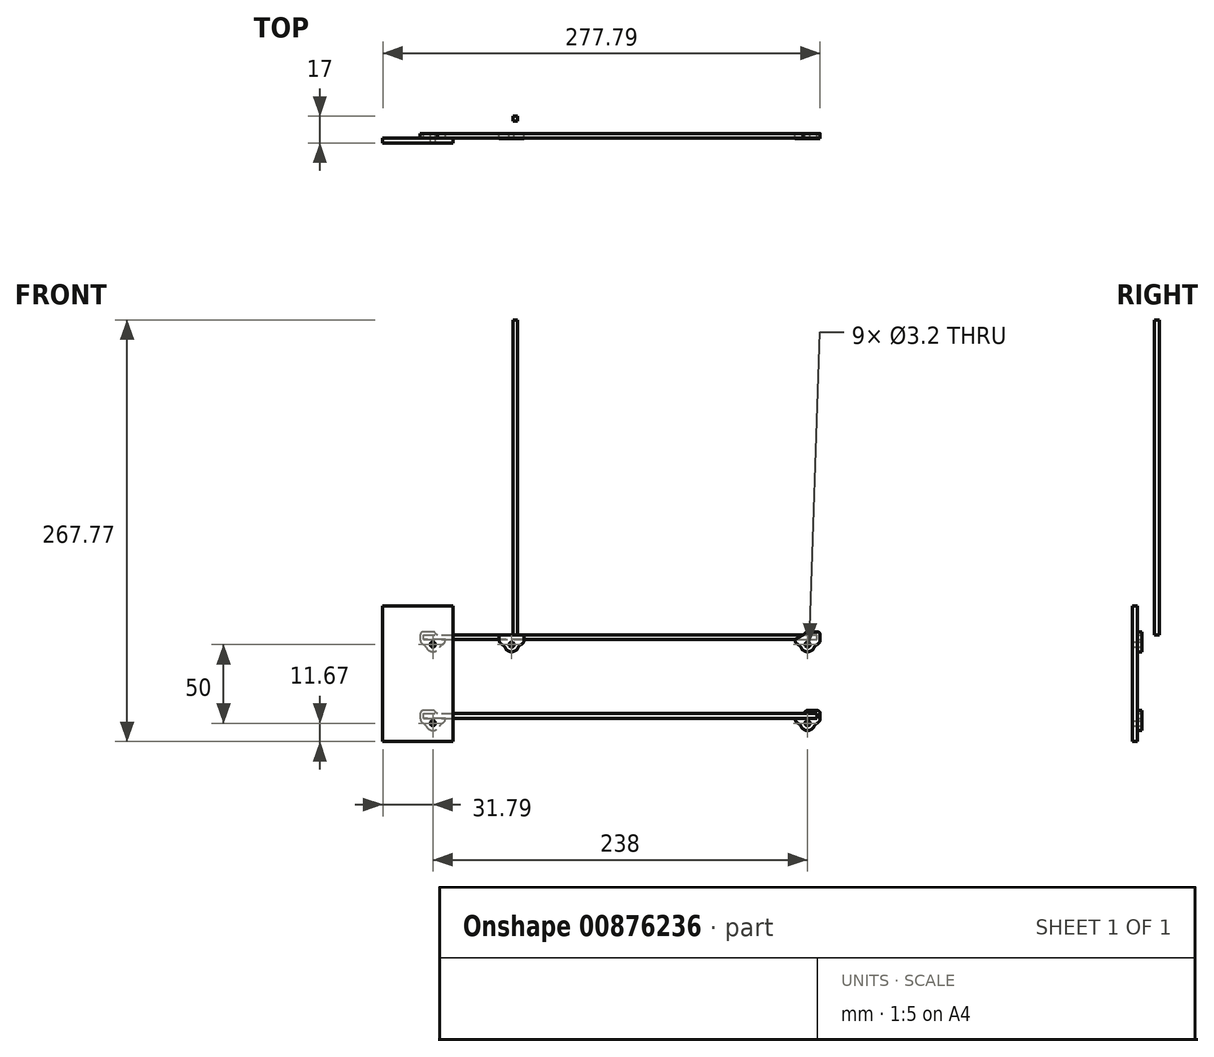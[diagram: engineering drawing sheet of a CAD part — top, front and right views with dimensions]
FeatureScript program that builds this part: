
annotation { "Feature Type Name" : "Feature", "Feature Type Description" : "" }
export const myFeature = defineFeature(function(context is Context, id is Id, definition is map)
    precondition{}
    {
        {
            var Q0;
            Q0=qCreatedBy(makeId("Front.planeOp"),FACE);
            var sketch = newSketch(context, id + "F0", { "sketchPlane" : qUnion([Q0])});
            skLineSegment(sketch, "E0", {"start": v(0, 0) * mm, "end": v(-238, 0) * mm});
            skLineSegment(sketch, "E1", {"start": v(0, -50) * mm, "end": v(-238, -50) * mm});
            skLineSegment(sketch, "E2", {"start": v(-238, -50) * mm, "end": v(-238, 188) * mm});
            skLineSegment(sketch, "E3", {"start": v(-188, 0) * mm, "end": v(-188, 188) * mm});
            skLineSegment(sketch, "E4", {"start": v(-188, 188) * mm, "end": v(-238, 188) * mm, "construction": true});
            skLineSegment(sketch, "E5", {"start": v(0, -50) * mm, "end": v(0, 0) * mm, "construction": true});
            skLineSegment(sketch, "E6", {"start": v(-188, 188) * mm, "end": v(-426, 188) * mm});
            skLineSegment(sketch, "E7", {"start": v(0, 0) * mm, "end": v(-188, 0) * mm});
            skSolve(sketch);
        }
        {
            var Q0;
            Q0=qCreatedBy(makeId("Front.planeOp"),FACE);
            var sketch = newSketch(context, id + "F1", { "sketchPlane" : qUnion([Q0])});
            skCircle(sketch, "E8", {"center": v(0, 0) * mm, "radius": 1.6 * mm});
            skArc(sketch, "E9", {"start": v(-4.15, -1.98) * mm, "mid": v(-2.46, -3.89) * mm, "end": v(0, -4.6) * mm});
            skLineSegment(sketch, "E10", {"start": v(-8, 3.1) * mm, "end": v(0, 3.1) * mm});
            skArc(sketch, "E11", {"start": v(-4.15, -1.98) * mm, "mid": v(-4.96, -0.83) * mm, "end": v(-6.09, 0) * mm});
            skArc(sketch, "E12", {"start": v(-6.09, 0) * mm, "mid": v(-7.48, 1.28) * mm, "end": v(-8, 3.1) * mm});
            skLineSegment(sketch, "E13.MirrorCS", {"start": v(8, 3.1) * mm, "end": v(0, 3.1) * mm});
            skArc(sketch, "E14.MirrorCS", {"start": v(6.09, 0) * mm, "mid": v(7.48, 1.28) * mm, "end": v(8, 3.1) * mm});
            skArc(sketch, "E15.MirrorCS", {"start": v(4.15, -1.98) * mm, "mid": v(4.96, -0.83) * mm, "end": v(6.09, 0) * mm});
            skArc(sketch, "E16.MirrorCS", {"start": v(4.15, -1.98) * mm, "mid": v(2.46, -3.89) * mm, "end": v(0, -4.6) * mm});
            skSolve(sketch);
        }
        {
            var Q0;
            Q0=makeQuery(id+"F1.imprint","IMPRINT",FACE,{"disambiguationData":[TD([[makeQuery(id+"F1.imprint","IMPRINT",EDGE,{"derivedFrom":sQuery(id+"F1.wireOp",EDGE,"E8")}),-1.0]])]});
            extrude(context, id + "F2", {"entities" : qUnion([Q0]), "depth" : 3 * mm, "offsetDistance" : 25 * mm});
        }
        {
            var Q0;
            Q0=qCreatedBy(makeId("Front.planeOp"),FACE);
            var sketch = newSketch(context, id + "F3", { "sketchPlane" : qUnion([Q0])});
            skCircle(sketch, "E17", {"center": v(0, 0) * mm, "radius": 1.6 * mm});
            skLineSegment(sketch, "E18", {"start": v(-8, 3.1) * mm, "end": v(6, 3.1) * mm});
            skLineSegment(sketch, "E19", {"start": v(6, 3.1) * mm, "end": v(6, 6.1) * mm});
            skLineSegment(sketch, "E20", {"start": v(6, 6.1) * mm, "end": v(-2.83, 6.1) * mm});
            skLineSegment(sketch, "E21", {"start": v(0, 8.1) * mm, "end": v(6, 8.1) * mm});
            skArc(sketch, "E22", {"start": v(8, 6.1) * mm, "mid": v(7.41, 7.51) * mm, "end": v(6, 8.1) * mm});
            skArc(sketch, "E23.0", {"start": v(-6.09, 0) * mm, "mid": v(-7.48, 1.28) * mm, "end": v(-8, 3.1) * mm});
            skArc(sketch, "E23.1", {"start": v(-4.15, -1.98) * mm, "mid": v(-4.96, -0.83) * mm, "end": v(-6.09, 0) * mm});
            skArc(sketch, "E23.2", {"start": v(-4.15, -1.98) * mm, "mid": v(-2.46, -3.89) * mm, "end": v(0, -4.6) * mm});
            skArc(sketch, "E24", {"start": v(0, 8.1) * mm, "mid": v(-0.77, 7.95) * mm, "end": v(-1.41, 7.51) * mm});
            skLineSegment(sketch, "E25", {"start": v(-1.41, 7.51) * mm, "end": v(-2.83, 6.1) * mm});
            skArc(sketch, "E26.0", {"start": v(4.15, -1.98) * mm, "mid": v(2.46, -3.89) * mm, "end": v(0, -4.6) * mm});
            skArc(sketch, "E26.1", {"start": v(4.15, -1.98) * mm, "mid": v(4.96, -0.83) * mm, "end": v(6.09, 0) * mm});
            skArc(sketch, "E26.2", {"start": v(6.09, 0) * mm, "mid": v(7.48, 1.28) * mm, "end": v(8, 3.1) * mm});
            skLineSegment(sketch, "E27", {"start": v(8, 6.1) * mm, "end": v(8, 3.1) * mm});
            skPoint(sketch, "E28.0", {"position": v(-119, 0) * mm});
            skPoint(sketch, "E28.1", {"position": v(-119, -50) * mm});
            skLineSegment(sketch, "E29", {"start": v(-119, 0) * mm, "end": v(-119, -50) * mm, "construction": true});
            skLineSegment(sketch, "E30.MirrorCS", {"start": v(-236.59, 7.51) * mm, "end": v(-235.17, 6.1) * mm});
            skCircle(sketch, "E31.MirrorC", {"center": v(-238, 0) * mm, "radius": 1.6 * mm});
            skLineSegment(sketch, "E32.MirrorCS", {"start": v(-244, 3.1) * mm, "end": v(-244, 6.1) * mm});
            skArc(sketch, "E33.MirrorCS", {"start": v(-242.15, -1.98) * mm, "mid": v(-242.96, -0.83) * mm, "end": v(-244.09, 0) * mm});
            skLineSegment(sketch, "E34.MirrorCS", {"start": v(-246, 6.1) * mm, "end": v(-246, 3.1) * mm});
            skArc(sketch, "E35.MirrorCS", {"start": v(-231.91, 0) * mm, "mid": v(-230.52, 1.28) * mm, "end": v(-230, 3.1) * mm});
            skArc(sketch, "E36.MirrorCS", {"start": v(-238, 8.1) * mm, "mid": v(-237.23, 7.95) * mm, "end": v(-236.59, 7.51) * mm});
            skArc(sketch, "E37.MirrorCS", {"start": v(-244.09, 0) * mm, "mid": v(-245.48, 1.28) * mm, "end": v(-246, 3.1) * mm});
            skArc(sketch, "E38.MirrorCS", {"start": v(-233.85, -1.98) * mm, "mid": v(-233.04, -0.83) * mm, "end": v(-231.91, 0) * mm});
            skArc(sketch, "E39.MirrorCS", {"start": v(-246, 6.1) * mm, "mid": v(-245.41, 7.51) * mm, "end": v(-244, 8.1) * mm});
            skLineSegment(sketch, "E40.MirrorCS", {"start": v(-244, 6.1) * mm, "end": v(-235.17, 6.1) * mm});
            skLineSegment(sketch, "E41.MirrorCS", {"start": v(-238, 8.1) * mm, "end": v(-244, 8.1) * mm});
            skLineSegment(sketch, "E42.MirrorCS", {"start": v(-230, 3.1) * mm, "end": v(-244, 3.1) * mm});
            skArc(sketch, "E43.MirrorCS", {"start": v(-233.85, -1.98) * mm, "mid": v(-235.54, -3.89) * mm, "end": v(-238, -4.6) * mm});
            skArc(sketch, "E44.MirrorCS", {"start": v(-242.15, -1.98) * mm, "mid": v(-240.46, -3.89) * mm, "end": v(-238, -4.6) * mm});
            skSolve(sketch);
        }
        {
            var Q0;
            Q0=makeQuery(id+"F3.imprint","IMPRINT",FACE,{"disambiguationData":[TD([[makeQuery(id+"F3.imprint","IMPRINT",EDGE,{"derivedFrom":sQuery(id+"F3.wireOp",EDGE,"E17")}),-1.0]])]});
            extrude(context, id + "F4", {"entities" : qUnion([Q0]), "depth" : 3 * mm, "offsetDistance" : 25 * mm});
        }
        {
            var Q0;
            Q0=makeQuery(id+"F3.imprint","IMPRINT",FACE,{"disambiguationData":[TD([[makeQuery(id+"F3.imprint","IMPRINT",EDGE,{"derivedFrom":sQuery(id+"F3.wireOp",EDGE,"E30.MirrorCS")}),-1.0]])]});
            var Q1;
            Q1=makeQuery(id+"F4.opExtrude","CAP_FACE",FACE,{"disambiguationData":[OSD([sQuery(id+"F3.wireOp",EDGE,"E17"),sQuery(id+"F3.wireOp",EDGE,"E18"),sQuery(id+"F3.wireOp",EDGE,"E19"),sQuery(id+"F3.wireOp",EDGE,"E20"),sQuery(id+"F3.wireOp",EDGE,"E21"),sQuery(id+"F3.wireOp",EDGE,"E22"),sQuery(id+"F3.wireOp",EDGE,"E23.0"),sQuery(id+"F3.wireOp",EDGE,"E23.1"),sQuery(id+"F3.wireOp",EDGE,"E23.2"),sQuery(id+"F3.wireOp",EDGE,"E24"),sQuery(id+"F3.wireOp",EDGE,"E25"),sQuery(id+"F3.wireOp",EDGE,"E26.0"),sQuery(id+"F3.wireOp",EDGE,"E26.1"),sQuery(id+"F3.wireOp",EDGE,"E26.2"),sQuery(id+"F3.wireOp",EDGE,"E27")])],"isStart":false});
            extrude(context, id + "F5", {"entities" : qUnion([Q0]), "endBound" : BoundingType.UP_TO_SURFACE, "depth" : 25 * mm, "endBoundEntityFace" : qUnion([Q1]), "offsetDistance" : 25 * mm});
        }
        {
            var Q0;
            Q0=makeQuery(id+"F4.opExtrude","SWEPT_FACE",FACE,{"disambiguationData":[OSD([sQuery(id+"F3.wireOp",EDGE,"E19")])]});
            extrude(context, id + "F6", {"entities" : qUnion([Q0]), "depth" : 250 * mm, "offsetDistance" : 25 * mm});
        }
        {
            var Q0;
            Q0=makeQuery(id+"F4.opExtrude","SWEPT_BODY",BODY,{"disambiguationData":[OSD([sQuery(id+"F3.wireOp",EDGE,"E17"),sQuery(id+"F3.wireOp",EDGE,"E18"),sQuery(id+"F3.wireOp",EDGE,"E19"),sQuery(id+"F3.wireOp",EDGE,"E20"),sQuery(id+"F3.wireOp",EDGE,"E21"),sQuery(id+"F3.wireOp",EDGE,"E22"),sQuery(id+"F3.wireOp",EDGE,"E23.0"),sQuery(id+"F3.wireOp",EDGE,"E23.1"),sQuery(id+"F3.wireOp",EDGE,"E23.2"),sQuery(id+"F3.wireOp",EDGE,"E24"),sQuery(id+"F3.wireOp",EDGE,"E25"),sQuery(id+"F3.wireOp",EDGE,"E26.0"),sQuery(id+"F3.wireOp",EDGE,"E26.1"),sQuery(id+"F3.wireOp",EDGE,"E26.2"),sQuery(id+"F3.wireOp",EDGE,"E27")])]});
            var Q1;
            Q1=makeQuery(id+"F5.opExtrude","SWEPT_BODY",BODY,{"disambiguationData":[OSD([sQuery(id+"F3.wireOp",EDGE,"E30.MirrorCS"),sQuery(id+"F3.wireOp",EDGE,"E31.MirrorC"),sQuery(id+"F3.wireOp",EDGE,"E32.MirrorCS"),sQuery(id+"F3.wireOp",EDGE,"E33.MirrorCS"),sQuery(id+"F3.wireOp",EDGE,"E34.MirrorCS"),sQuery(id+"F3.wireOp",EDGE,"E35.MirrorCS"),sQuery(id+"F3.wireOp",EDGE,"E36.MirrorCS"),sQuery(id+"F3.wireOp",EDGE,"E37.MirrorCS"),sQuery(id+"F3.wireOp",EDGE,"E38.MirrorCS"),sQuery(id+"F3.wireOp",EDGE,"E39.MirrorCS"),sQuery(id+"F3.wireOp",EDGE,"E40.MirrorCS"),sQuery(id+"F3.wireOp",EDGE,"E41.MirrorCS"),sQuery(id+"F3.wireOp",EDGE,"E42.MirrorCS"),sQuery(id+"F3.wireOp",EDGE,"E43.MirrorCS"),sQuery(id+"F3.wireOp",EDGE,"E44.MirrorCS")])]});
            var Q2;
            Q2=sQuery(id+"F0.wireOp",EDGE,"E5");
            transform(context, id + "F7", {"entities" : qUnion([Q0, Q1]), "transformType" : TransformType.TRANSLATION_ENTITY, "oppositeDirectionEntity" : true, "transformLine" : qUnion([Q2]), "makeCopy" : true});
        }
        {
            var Q0;
            Q0=makeQuery(id+"F6.opExtrude","SWEPT_BODY",BODY,{"disambiguationData":[OSD([sQuery(id+"F3.wireOp",EDGE,"E19")])]});
            var Q1;
            Q1=sQuery(id+"F0.wireOp",EDGE,"E5");
            transform(context, id + "F8", {"entities" : qUnion([Q0]), "transformType" : TransformType.TRANSLATION_ENTITY, "oppositeDirectionEntity" : true, "transformLine" : qUnion([Q1]), "makeCopy" : true});
        }
        {
            var Q0;
            Q0=makeQuery(id+"F2.opExtrude","SWEPT_BODY",BODY,{"disambiguationData":[OSD([sQuery(id+"F1.wireOp",EDGE,"E8"),sQuery(id+"F1.wireOp",EDGE,"E9"),sQuery(id+"F1.wireOp",EDGE,"E10"),sQuery(id+"F1.wireOp",EDGE,"E11"),sQuery(id+"F1.wireOp",EDGE,"E12"),sQuery(id+"F1.wireOp",EDGE,"E13.MirrorCS"),sQuery(id+"F1.wireOp",EDGE,"E14.MirrorCS"),sQuery(id+"F1.wireOp",EDGE,"E15.MirrorCS"),sQuery(id+"F1.wireOp",EDGE,"E16.MirrorCS")])]});
            var Q1;
            Q1=sQuery(id+"F0.wireOp",EDGE,"E7");
            transform(context, id + "F9", {"entities" : qUnion([Q0]), "transformType" : TransformType.TRANSLATION_ENTITY, "oppositeDirectionEntity" : false, "transformLine" : qUnion([Q1]), "makeCopy" : false});
        }
        {
            var Q0;
            Q0=makeQuery(id+"F6.opExtrude","SWEPT_FACE",FACE,{"disambiguationData":[OSD([sQuery(id+"F3.wireOp",EDGE,"E19"),sQuery(id+"F3.wireOp",EDGE,"E20")])]});
            var sketch = newSketch(context, id + "F10", { "sketchPlane" : qUnion([Q0])});
            skLineSegment(sketch, "E45.bottom", {"start": v(-184.2, 8) * mm, "end": v(-187.2, 8) * mm});
            skLineSegment(sketch, "E45.top", {"start": v(-184.2, 11) * mm, "end": v(-187.2, 11) * mm});
            skLineSegment(sketch, "E45.left", {"start": v(-184.2, 8) * mm, "end": v(-184.2, 11) * mm});
            skLineSegment(sketch, "E45.right", {"start": v(-187.2, 8) * mm, "end": v(-187.2, 11) * mm});
            skSolve(sketch);
        }
        {
            var Q0;
            Q0=makeQuery(id+"F10.imprint","IMPRINT",FACE,{"disambiguationData":[TD([[makeQuery(id+"F10.imprint","IMPRINT",EDGE,{"derivedFrom":sQuery(id+"F10.wireOp",EDGE,"E45.bottom")}),-1.0]])]});
            extrude(context, id + "F11", {"entities" : qUnion([Q0]), "depth" : 200 * mm, "offsetDistance" : 25 * mm});
        }
        {
            var Q0;
            Q0=makeQuery(id+"F5.opExtrude","CAP_FACE",FACE,{"disambiguationData":[OSD([sQuery(id+"F3.wireOp",EDGE,"E30.MirrorCS"),sQuery(id+"F3.wireOp",EDGE,"E31.MirrorC"),sQuery(id+"F3.wireOp",EDGE,"E32.MirrorCS"),sQuery(id+"F3.wireOp",EDGE,"E33.MirrorCS"),sQuery(id+"F3.wireOp",EDGE,"E34.MirrorCS"),sQuery(id+"F3.wireOp",EDGE,"E35.MirrorCS"),sQuery(id+"F3.wireOp",EDGE,"E36.MirrorCS"),sQuery(id+"F3.wireOp",EDGE,"E37.MirrorCS"),sQuery(id+"F3.wireOp",EDGE,"E38.MirrorCS"),sQuery(id+"F3.wireOp",EDGE,"E39.MirrorCS"),sQuery(id+"F3.wireOp",EDGE,"E40.MirrorCS"),sQuery(id+"F3.wireOp",EDGE,"E41.MirrorCS"),sQuery(id+"F3.wireOp",EDGE,"E42.MirrorCS"),sQuery(id+"F3.wireOp",EDGE,"E43.MirrorCS"),sQuery(id+"F3.wireOp",EDGE,"E44.MirrorCS")])],"isStart":false});
            var sketch = newSketch(context, id + "F12", { "sketchPlane" : qUnion([Q0])});
            skLineSegment(sketch, "E46.bottom", {"start": v(-225.1, -61.67) * mm, "end": v(-269.8, -61.67) * mm});
            skLineSegment(sketch, "E46.top", {"start": v(-225.1, 24.57) * mm, "end": v(-269.8, 24.57) * mm});
            skLineSegment(sketch, "E46.left", {"start": v(-225.1, -61.67) * mm, "end": v(-225.1, 24.57) * mm});
            skLineSegment(sketch, "E46.right", {"start": v(-269.8, -61.67) * mm, "end": v(-269.8, 24.57) * mm});
            skCircle(sketch, "E47.0", {"center": v(-238, 0) * mm, "radius": 1.6 * mm});
            skCircle(sketch, "E48.0", {"center": v(-238, -50) * mm, "radius": 1.6 * mm});
            skSolve(sketch);
        }
        {
            var Q0;
            Q0 = qSketchRegion(id + "F12", true);
            extrude(context, id + "F13", {"entities" : qUnion([Q0]), "depth" : 3 * mm, "offsetDistance" : 25 * mm});
        }
        {
            var Q0;
            Q0=makeQuery(id+"F4.opExtrude","CAP_FACE",FACE,{"disambiguationData":[OSD([sQuery(id+"F3.wireOp",EDGE,"E17"),sQuery(id+"F3.wireOp",EDGE,"E18"),sQuery(id+"F3.wireOp",EDGE,"E19"),sQuery(id+"F3.wireOp",EDGE,"E20"),sQuery(id+"F3.wireOp",EDGE,"E21"),sQuery(id+"F3.wireOp",EDGE,"E22"),sQuery(id+"F3.wireOp",EDGE,"E23.0"),sQuery(id+"F3.wireOp",EDGE,"E23.1"),sQuery(id+"F3.wireOp",EDGE,"E23.2"),sQuery(id+"F3.wireOp",EDGE,"E24"),sQuery(id+"F3.wireOp",EDGE,"E25"),sQuery(id+"F3.wireOp",EDGE,"E26.0"),sQuery(id+"F3.wireOp",EDGE,"E26.1"),sQuery(id+"F3.wireOp",EDGE,"E26.2"),sQuery(id+"F3.wireOp",EDGE,"E27")])],"isStart":false});
            var sketch = newSketch(context, id + "F14", { "sketchPlane" : qUnion([Q0])});
            skLineSegment(sketch, "E49.0.0", {"start": v(6, 8.1) * mm, "end": v(0, 8.1) * mm});
            skArc(sketch, "E49.0.1", {"start": v(0, 8.1) * mm, "mid": v(-0.77, 7.95) * mm, "end": v(-1.41, 7.51) * mm});
            skLineSegment(sketch, "E49.0.2", {"start": v(-1.41, 7.51) * mm, "end": v(-2.83, 6.1) * mm});
            skArc(sketch, "E49.0.6", {"start": v(-8, 3.1) * mm, "mid": v(-7.48, 1.28) * mm, "end": v(-6.09, 0) * mm});
            skArc(sketch, "E49.0.7", {"start": v(-6.09, 0) * mm, "mid": v(-4.96, -0.83) * mm, "end": v(-4.15, -1.98) * mm});
            skArc(sketch, "E49.0.8", {"start": v(-4.15, -1.98) * mm, "mid": v(0, -4.6) * mm, "end": v(4.15, -1.98) * mm});
            skArc(sketch, "E49.0.9", {"start": v(4.15, -1.98) * mm, "mid": v(4.96, -0.83) * mm, "end": v(6.09, 0) * mm});
            skArc(sketch, "E49.0.10", {"start": v(6.09, 0) * mm, "mid": v(7.48, 1.28) * mm, "end": v(8, 3.1) * mm});
            skLineSegment(sketch, "E49.0.11", {"start": v(8, 3.1) * mm, "end": v(8, 6.1) * mm});
            skArc(sketch, "E49.0.12", {"start": v(8, 6.1) * mm, "mid": v(7.41, 7.51) * mm, "end": v(6, 8.1) * mm});
            skLineSegment(sketch, "E50", {"start": v(-2.83, 6.1) * mm, "end": v(-8, 3.1) * mm});
            skCircle(sketch, "E51.0", {"center": v(0, 0) * mm, "radius": 1.6 * mm});
            skSolve(sketch);
        }
        {
            var Q0;
            Q0 = qSketchRegion(id + "F14", true);
            extrude(context, id + "F15", {"entities" : qUnion([Q0]), "depth" : 0.1 * mm, "offsetDistance" : 25 * mm});
        }
        {
            var Q0;
            Q0=makeQuery(id+"F2.opExtrude","CAP_FACE",FACE,{"disambiguationData":[OSD([sQuery(id+"F1.wireOp",EDGE,"E8"),sQuery(id+"F1.wireOp",EDGE,"E9"),sQuery(id+"F1.wireOp",EDGE,"E10"),sQuery(id+"F1.wireOp",EDGE,"E11"),sQuery(id+"F1.wireOp",EDGE,"E12"),sQuery(id+"F1.wireOp",EDGE,"E13.MirrorCS"),sQuery(id+"F1.wireOp",EDGE,"E14.MirrorCS"),sQuery(id+"F1.wireOp",EDGE,"E15.MirrorCS"),sQuery(id+"F1.wireOp",EDGE,"E16.MirrorCS")])],"isStart":false});
            var sketch = newSketch(context, id + "F16", { "sketchPlane" : qUnion([Q0])});
            skArc(sketch, "E52.0", {"start": v(-183.85, -1.98) * mm, "mid": v(-188, -4.6) * mm, "end": v(-192.15, -1.98) * mm});
            skArc(sketch, "E53.0", {"start": v(-183.85, -1.98) * mm, "mid": v(-183.04, -0.83) * mm, "end": v(-181.91, 0) * mm});
            skArc(sketch, "E54.0", {"start": v(-181.91, 0) * mm, "mid": v(-180.52, 1.28) * mm, "end": v(-180, 3.1) * mm});
            skArc(sketch, "E55.0", {"start": v(-194.09, 0) * mm, "mid": v(-195.48, 1.28) * mm, "end": v(-196, 3.1) * mm});
            skArc(sketch, "E56.0", {"start": v(-192.15, -1.98) * mm, "mid": v(-192.96, -0.83) * mm, "end": v(-194.09, 0) * mm});
            skLineSegment(sketch, "E57.0", {"start": v(-244, 6.1) * mm, "end": v(6, 6.1) * mm, "construction": true});
            skLineSegment(sketch, "E58", {"start": v(-196, 3.1) * mm, "end": v(-196, 6.1) * mm});
            skLineSegment(sketch, "E59", {"start": v(-180, 3.1) * mm, "end": v(-180, 6.1) * mm});
            skLineSegment(sketch, "E60", {"start": v(-180, 6.1) * mm, "end": v(-196, 6.1) * mm});
            skCircle(sketch, "E61.0", {"center": v(-188, 0) * mm, "radius": 1.6 * mm});
            skSolve(sketch);
        }
        {
            var Q0;
            Q0 = qSketchRegion(id + "F16", true);
            extrude(context, id + "F17", {"entities" : qUnion([Q0]), "depth" : 0.1 * mm, "offsetDistance" : 25 * mm});
        }
    });
